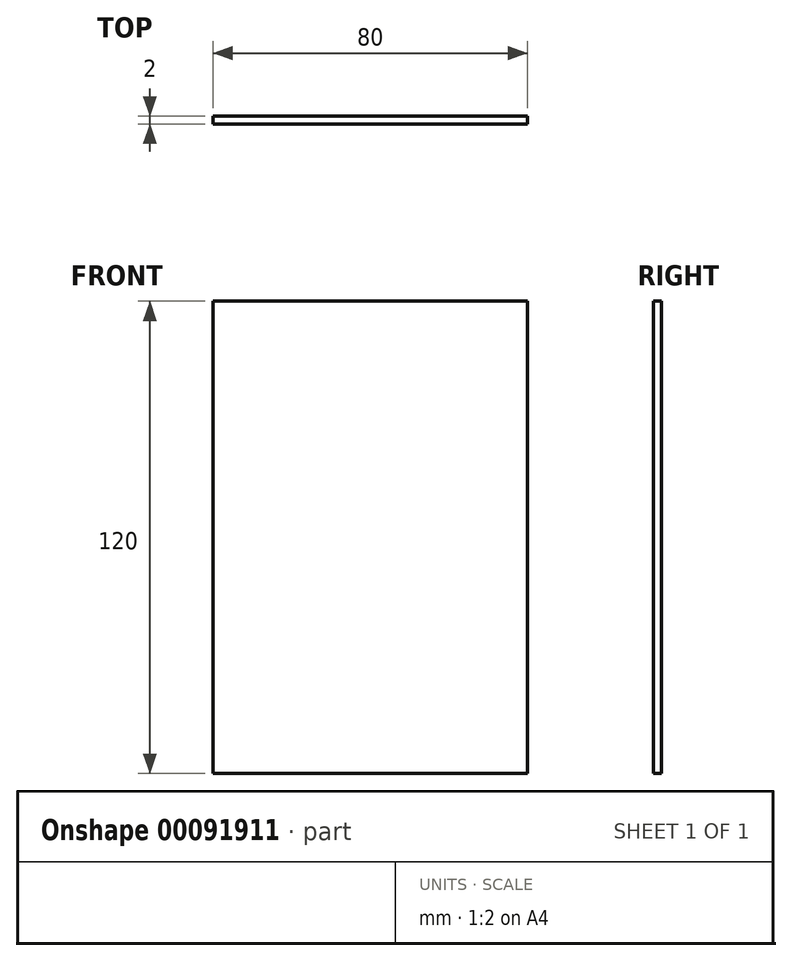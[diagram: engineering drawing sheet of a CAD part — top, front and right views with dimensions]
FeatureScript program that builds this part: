
annotation { "Feature Type Name" : "Feature", "Feature Type Description" : "" }
export const myFeature = defineFeature(function(context is Context, id is Id, definition is map)
    precondition{}
    {
        {
            var Q0;
            Q0=qCreatedBy(makeId("Front.planeOp"), FACE);
            var sketch = newSketch(context, id + "F0", { "sketchPlane" : qUnion([Q0])});
            skLineSegment(sketch, "E0.bottom", {"start": v(40, 60) * mm, "end": v(-40, 60) * mm});
            skLineSegment(sketch, "E0.top", {"start": v(40, -60) * mm, "end": v(-40, -60) * mm});
            skLineSegment(sketch, "E0.left", {"start": v(40, 60) * mm, "end": v(40, -60) * mm});
            skLineSegment(sketch, "E0.right", {"start": v(-40, 60) * mm, "end": v(-40, -60) * mm});
            skPoint(sketch, "E0.middle", {"position": v(0, 0) * mm});
            skSolve(sketch);
        }
        {
            var Q0;
            Q0 = qSketchRegion(id + "F0", true);
            extrude(context, id + "F1", {"entities" : qUnion([Q0]), "depth" : 2 * mm, "offsetDistance" : 25 * mm});
        }
    });
